# Revit family: Rouge_XO_Standard
name_source: partatom
category: Doors
revit_build: Autodesk Revit 2014 (Build: 20130308_1515(x64)
units: mm (PartAtom-declared; Revit-internal decimal feet)

## types (19) — shared parameters
Centered In Wall = Yes
Custom Door Height = 2090 mm  [stored 6.85696 ft]
Custom Sash Width Left = 600 mm
Description = Sliding door, XO
Equal Sash Width = Yes
Frame Thickness = 64 mm  [stored 0.209974 ft]
Heavy Duty Interlocker = No
Height = 2090 mm  [stored 6.85696 ft]
Limit Door Height Max = 2141 mm
Limit Door Height Min = 341 mm
Limit Door Width Min = 592 mm
Limit Sash Height Max = 2100 mm
Limit Sash Height Min = 300 mm  [stored 0.984252 ft]
Limit Sash Width Max = 1500 mm  [stored 4.92126 ft]
Limit Sash Width Min = 300 mm  [stored 0.984252 ft]
Manufacturer = Crealco
Model = Rouge
Rough Width = 3 mm  [stored 0.00984252 ft]
Sash Frame Seal = 4 mm  [stored 0.0131234 ft]
Sash Frame Side Gap = 4 mm  [stored 0.0131234 ft]
Sash Frame Top Gap = 10 mm  [stored 0.0328084 ft]
Sash Height = 2049 mm
Standard Interlocker = Yes
URL = http://www.crealco.co.za
Wall Closure = By host
zero-valued in all types: Custom Frame Offset From Exterior, Default Sill Height

## per-type parameters (varying)
| type | Area Left Sash Glazing | Area Right Sash Glazing | Custom Door Width | Custom Windload | Interlock Configuration Door | Interlock Configuration Exterior | Interlock Configuration Interior | Intruderprufe LowE SHGC Value | Intruderprufe LowE U Value | Intruderprufe SHGC Value | Intruderprufe U Value | Limit Door Width Max | Limit Sash Width Left Max | Limit Sash Width Left Min | Max Pane Area | Sash Width Left | Sash Width Right | Toughened Safety SHGC Value | Toughened Safety U Value | Width | Windload Design |
| Rouge-1521XO-1000Pa | 1.32 m² | 1.41 m² | 1490 mm  [stored 4.88845 ft] | 1000 mm  [stored 3.28084 ft] | 2 mm  [stored 0.00656168 ft] | 1 mm  [stored 0.00328084 ft] | 2 mm  [stored 0.00656168 ft] | 0.646 | 4.33 | 0.738 | 5.82 | 2990 mm  [stored 9.80971 ft] | 1198 mm | 300 mm  [stored 0.984252 ft] | 1.41 m² | 749 mm | 749 mm | 0.77 | 5.89 | 1490 mm  [stored 4.88845 ft] | 1000 mm  [stored 3.28084 ft] |
| Rouge-1521XO-1500Pa | 1.32 m² | 1.41 m² | 1490 mm  [stored 4.88845 ft] | 1500 mm  [stored 4.92126 ft] | 4 mm  [stored 0.0131234 ft] | 2 mm  [stored 0.00656168 ft] | 2 mm  [stored 0.00656168 ft] | 0.646 | 4.33 | 0.738 | 5.82 | 2990 mm  [stored 9.80971 ft] | 1198 mm | 300 mm  [stored 0.984252 ft] | 1.41 m² | 749 mm | 749 mm | 0.77 | 5.89 | 1490 mm  [stored 4.88845 ft] | 1500 mm  [stored 4.92126 ft] |
| Rouge-1521XO-2000Pa | 1.32 m² | 1.41 m² | 1490 mm  [stored 4.88845 ft] | 2000 mm  [stored 6.56168 ft] | 3 mm  [stored 0.00984252 ft] | 1 mm  [stored 0.00328084 ft] | 3 mm  [stored 0.00984252 ft] | 0.646 | 4.33 | 0.738 | 5.82 | 2390 mm  [stored 7.84121 ft] | 1198 mm | 300 mm  [stored 0.984252 ft] | 1.41 m² | 749 mm | 749 mm | 0.77 | 5.89 | 1490 mm  [stored 4.88845 ft] | 2000 mm  [stored 6.56168 ft] |
| Rouge-1821XO-1000Pa | 1.61 m² | 1.71 m² | 1790 mm  [stored 5.8727 ft] | 1000 mm  [stored 3.28084 ft] | 2 mm  [stored 0.00656168 ft] | 1 mm  [stored 0.00328084 ft] | 2 mm  [stored 0.00656168 ft] | 0.653 | 4.23 | 0.745 | 5.79 | 2990 mm  [stored 9.80971 ft] | 1498 mm | 300 mm  [stored 0.984252 ft] | 1.71 m² | 899 mm | 899 mm | 0.778 | 5.87 | 1790 mm  [stored 5.8727 ft] | 1000 mm  [stored 3.28084 ft] |
| Rouge-1821XO-1500Pa | 1.61 m² | 1.71 m² | 1790 mm  [stored 5.8727 ft] | 1500 mm  [stored 4.92126 ft] | 3 mm  [stored 0.00984252 ft] | 1 mm  [stored 0.00328084 ft] | 3 mm  [stored 0.00984252 ft] | 0.653 | 4.23 | 0.745 | 5.79 | 2990 mm  [stored 9.80971 ft] | 1498 mm | 300 mm  [stored 0.984252 ft] | 1.71 m² | 899 mm | 899 mm | 0.778 | 5.87 | 1790 mm  [stored 5.8727 ft] | 1500 mm  [stored 4.92126 ft] |
| Rouge-1821XO-2000Pa | 1.61 m² | 1.71 m² | 1790 mm  [stored 5.8727 ft] | 2000 mm  [stored 6.56168 ft] | 6 mm  [stored 0.019685 ft] | 3 mm  [stored 0.00984252 ft] | 3 mm  [stored 0.00984252 ft] | 0.653 | 4.23 | 0.745 | 5.79 | 2390 mm  [stored 7.84121 ft] | 1498 mm | 300 mm  [stored 0.984252 ft] | 1.71 m² | 899 mm | 899 mm | 0.778 | 5.87 | 1790 mm  [stored 5.8727 ft] | 2000 mm  [stored 6.56168 ft] |
| Rouge-2021XO-1000Pa | 1.81 m² | 1.9 m² | 1990 mm  [stored 6.52887 ft] | 1000 mm  [stored 3.28084 ft] | 4 mm  [stored 0.0131234 ft] | 2 mm  [stored 0.00656168 ft] | 2 mm  [stored 0.00656168 ft] | 0.656 | 4.17 | 0.749 | 5.78 | 2990 mm  [stored 9.80971 ft] | 1500 mm  [stored 4.92126 ft] | 498 mm | 1.9 m² | 999 mm | 999 mm | 0.782 | 5.85 | 1990 mm  [stored 6.52887 ft] | 1000 mm  [stored 3.28084 ft] |
| Rouge-2021XO-1500Pa | 1.81 m² | 1.9 m² | 1990 mm  [stored 6.52887 ft] | 1500 mm  [stored 4.92126 ft] | 3 mm  [stored 0.00984252 ft] | 1 mm  [stored 0.00328084 ft] | 3 mm  [stored 0.00984252 ft] | 0.656 | 4.17 | 0.749 | 5.78 | 2990 mm  [stored 9.80971 ft] | 1500 mm  [stored 4.92126 ft] | 498 mm | 1.9 m² | 999 mm | 999 mm | 0.782 | 5.85 | 1990 mm  [stored 6.52887 ft] | 1500 mm  [stored 4.92126 ft] |
| Rouge-2021XO-2000Pa | 1.81 m² | 1.9 m² | 1990 mm  [stored 6.52887 ft] | 2000 mm  [stored 6.56168 ft] | 6 mm  [stored 0.019685 ft] | 3 mm  [stored 0.00984252 ft] | 3 mm  [stored 0.00984252 ft] | 0.656 | 4.17 | 0.749 | 5.78 | 2390 mm  [stored 7.84121 ft] | 1500 mm  [stored 4.92126 ft] | 498 mm | 1.9 m² | 999 mm | 999 mm | 0.782 | 5.85 | 1990 mm  [stored 6.52887 ft] | 2000 mm  [stored 6.56168 ft] |
| Rouge-2121XO-1000Pa | 1.91 m² | 2 m² | 2090 mm  [stored 6.85696 ft] | 1000 mm  [stored 3.28084 ft] | 4 mm  [stored 0.0131234 ft] | 2 mm  [stored 0.00656168 ft] | 2 mm  [stored 0.00656168 ft] | 0.657 | 4.15 | 0.75 | 5.77 | 2990 mm  [stored 9.80971 ft] | 1500 mm  [stored 4.92126 ft] | 598 mm | 2 m² | 1049 mm | 1049 mm | 0.783 | 5.85 | 2090 mm  [stored 6.85696 ft] | 1000 mm  [stored 3.28084 ft] |
| Rouge-2121XO-1500Pa | 1.91 m² | 2 m² | 2090 mm  [stored 6.85696 ft] | 1500 mm  [stored 4.92126 ft] | 3 mm  [stored 0.00984252 ft] | 1 mm  [stored 0.00328084 ft] | 3 mm  [stored 0.00984252 ft] | 0.657 | 4.15 | 0.75 | 5.77 | 2990 mm  [stored 9.80971 ft] | 1500 mm  [stored 4.92126 ft] | 598 mm | 2 m² | 1049 mm | 1049 mm | 0.783 | 5.85 | 2090 mm  [stored 6.85696 ft] | 1500 mm  [stored 4.92126 ft] |
| Rouge-2121XO-2000Pa | 1.91 m² | 2 m² | 2090 mm  [stored 6.85696 ft] | 2000 mm  [stored 6.56168 ft] | 6 mm  [stored 0.019685 ft] | 3 mm  [stored 0.00984252 ft] | 3 mm  [stored 0.00984252 ft] | 0.657 | 4.15 | 0.75 | 5.77 | 2390 mm  [stored 7.84121 ft] | 1500 mm  [stored 4.92126 ft] | 598 mm | 2 m² | 1049 mm | 1049 mm | 0.783 | 5.85 | 2090 mm  [stored 6.85696 ft] | 2000 mm  [stored 6.56168 ft] |
| Rouge-2421XO-1000Pa | 2.2 m² | 2.3 m² | 2390 mm  [stored 7.84121 ft] | 1000 mm  [stored 3.28084 ft] | 4 mm  [stored 0.0131234 ft] | 2 mm  [stored 0.00656168 ft] | 2 mm  [stored 0.00656168 ft] | 0.66 | 4.09 | 0.754 | 5.76 | 2990 mm  [stored 9.80971 ft] | 1500 mm  [stored 4.92126 ft] | 898 mm | 2.3 m² | 1199 mm | 1199 mm | 0.787 | 5.83 | 2390 mm  [stored 7.84121 ft] | 1000 mm  [stored 3.28084 ft] |
| Rouge-2421XO-1500Pa | 2.2 m² | 2.3 m² | 2390 mm  [stored 7.84121 ft] | 1500 mm  [stored 4.92126 ft] | 5 mm  [stored 0.0164042 ft] | 2 mm  [stored 0.00656168 ft] | 3 mm  [stored 0.00984252 ft] | 0.66 | 4.09 | 0.754 | 5.76 | 2990 mm  [stored 9.80971 ft] | 1500 mm  [stored 4.92126 ft] | 898 mm | 2.3 m² | 1199 mm | 1199 mm | 0.787 | 5.83 | 2390 mm  [stored 7.84121 ft] | 1500 mm  [stored 4.92126 ft] |
| Rouge-2421XO-2000Pa | 2.2 m² | 2.3 m² | 2390 mm  [stored 7.84121 ft] | 2000 mm  [stored 6.56168 ft] | 6 mm  [stored 0.019685 ft] | 3 mm  [stored 0.00984252 ft] | 3 mm  [stored 0.00984252 ft] | 0.66 | 4.09 | 0.754 | 5.76 | 2390 mm  [stored 7.84121 ft] | 1500 mm  [stored 4.92126 ft] | 898 mm | 2.3 m² | 1199 mm | 1199 mm | 0.787 | 5.83 | 2390 mm  [stored 7.84121 ft] | 2000 mm  [stored 6.56168 ft] |
| Rouge-2721XO-1000Pa | 2.5 m² | 2.59 m² | 2690 mm | 1000 mm  [stored 3.28084 ft] | 3 mm  [stored 0.00984252 ft] | 1 mm  [stored 0.00328084 ft] | 3 mm  [stored 0.00984252 ft] | 0.663 | 4.08 | 0.758 | 5.78 | 2990 mm  [stored 9.80971 ft] | 1500 mm  [stored 4.92126 ft] | 1198 mm | 2.59 m² | 1349 mm | 1349 mm | 0.791 | 5.85 | 2690 mm | 1000 mm  [stored 3.28084 ft] |
| Rouge-2721XO-1500Pa | 2.5 m² | 2.59 m² | 2690 mm | 1500 mm  [stored 4.92126 ft] | 6 mm  [stored 0.019685 ft] | 3 mm  [stored 0.00984252 ft] | 3 mm  [stored 0.00984252 ft] | 0.663 | 4.08 | 0.758 | 5.78 | 2990 mm  [stored 9.80971 ft] | 1500 mm  [stored 4.92126 ft] | 1198 mm | 2.59 m² | 1349 mm | 1349 mm | 0.791 | 5.85 | 2690 mm | 1500 mm  [stored 4.92126 ft] |
| Rouge-3021XO-1000Pa | 2.79 m² | 2.89 m² | 2990 mm  [stored 9.80971 ft] | 1000 mm  [stored 3.28084 ft] | 3 mm  [stored 0.00984252 ft] | 1 mm  [stored 0.00328084 ft] | 3 mm  [stored 0.00984252 ft] | 0.665 | 4.04 | 0.76 | 5.76 | 2990 mm  [stored 9.80971 ft] | 1500 mm  [stored 4.92126 ft] | 1498 mm | 2.89 m² | 1499 mm | 1499 mm | 0.793 | 5.84 | 2990 mm  [stored 9.80971 ft] | 1000 mm  [stored 3.28084 ft] |
| Rouge-3021XO-1500Pa | 2.79 m² | 2.89 m² | 2990 mm  [stored 9.80971 ft] | 1500 mm  [stored 4.92126 ft] | 6 mm  [stored 0.019685 ft] | 3 mm  [stored 0.00984252 ft] | 3 mm  [stored 0.00984252 ft] | 0.665 | 4.04 | 0.76 | 5.76 | 2990 mm  [stored 9.80971 ft] | 1500 mm  [stored 4.92126 ft] | 1498 mm | 2.89 m² | 1499 mm | 1499 mm | 0.793 | 5.84 | 2990 mm  [stored 9.80971 ft] | 1500 mm  [stored 4.92126 ft] |

note: [stored X ft] marks values corroborated as IEEE doubles in the binary element streams (Revit-internal decimal feet)

## geometry (parser evidence)
native form markers: Sweep x40
no freeform markers — native parametric forms only
